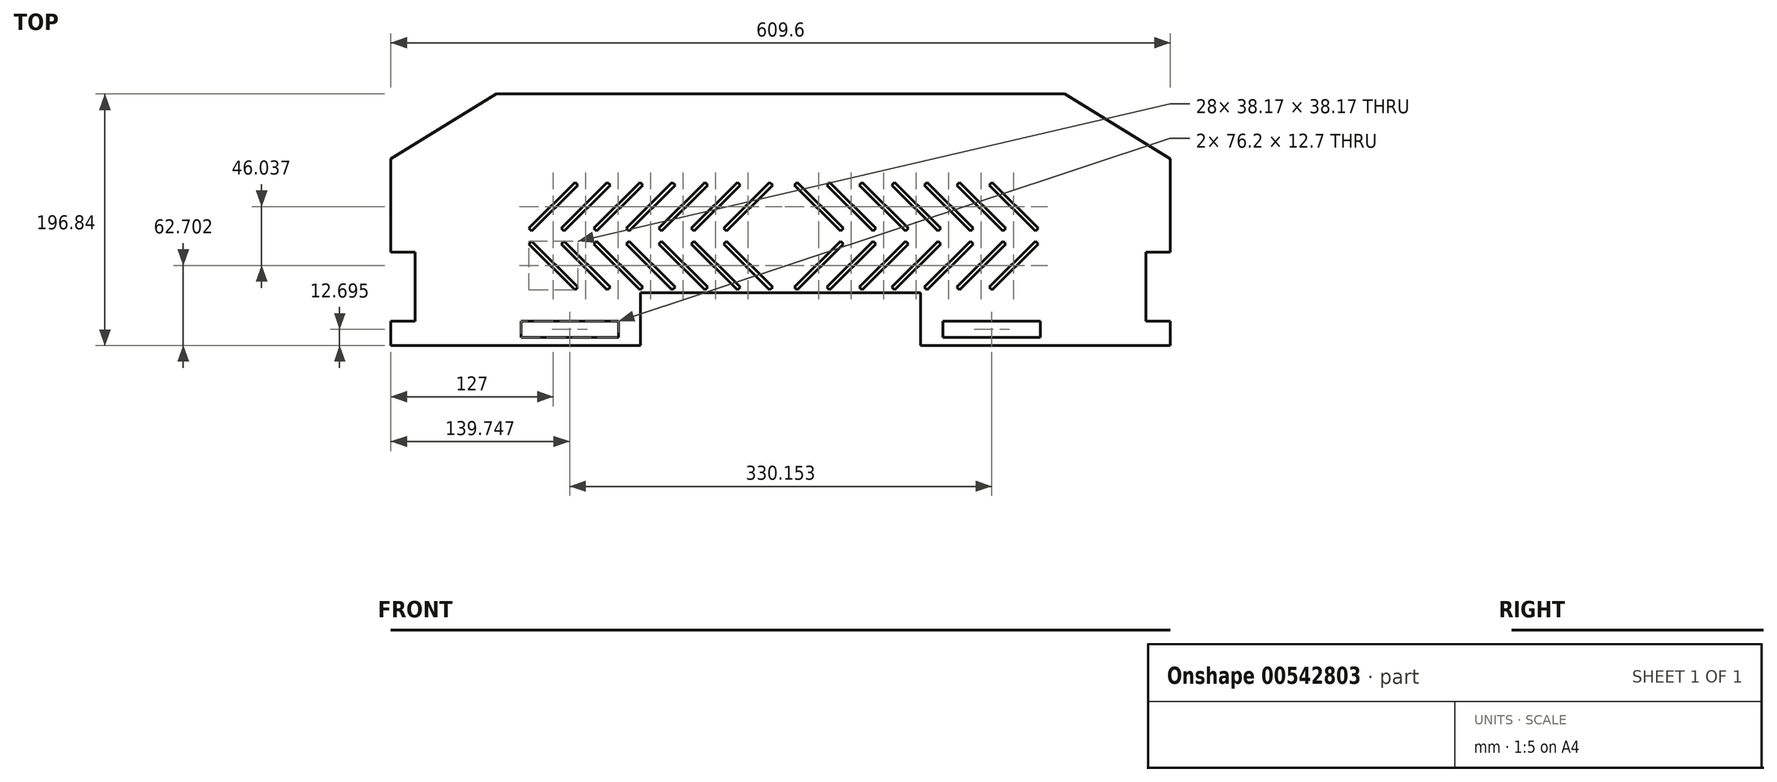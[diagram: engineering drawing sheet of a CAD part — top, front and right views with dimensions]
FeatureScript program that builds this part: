
annotation { "Feature Type Name" : "Feature", "Feature Type Description" : "" }
export const myFeature = defineFeature(function(context is Context, id is Id, definition is map)
    precondition{}
    {
        {
            var Q0;
            Q0=qCreatedBy(makeId("Top.planeOp"),FACE);
            var sketch = newSketch(context, id + "F0", { "sketchPlane" : qUnion([Q0])});
            skLineSegment(sketch, "E0", {"start": v(304.8, -19.05) * mm, "end": v(304.8, 53.97) * mm});
            skLineSegment(sketch, "E1", {"start": v(304.8, 53.97) * mm, "end": v(222.25, 104.77) * mm});
            skLineSegment(sketch, "E2", {"start": v(222.25, 104.77) * mm, "end": v(-222.25, 104.77) * mm});
            skLineSegment(sketch, "E3", {"start": v(-222.25, 104.77) * mm, "end": v(-304.8, 53.97) * mm});
            skLineSegment(sketch, "E4", {"start": v(-304.8, 53.97) * mm, "end": v(-304.8, -19.05) * mm});
            skLineSegment(sketch, "E5", {"start": v(-304.8, -19.05) * mm, "end": v(-285.75, -19.05) * mm});
            skLineSegment(sketch, "E6", {"start": v(-285.75, -19.05) * mm, "end": v(-285.75, -73.02) * mm});
            skLineSegment(sketch, "E7", {"start": v(-285.75, -73.02) * mm, "end": v(-304.8, -73.02) * mm});
            skLineSegment(sketch, "E8", {"start": v(-304.8, -73.02) * mm, "end": v(-304.8, -104.77) * mm});
            skLineSegment(sketch, "E9", {"start": v(-304.8, -104.77) * mm, "end": v(-109.54, -104.77) * mm});
            skLineSegment(sketch, "E10", {"start": v(-109.54, -104.77) * mm, "end": v(-109.54, -50.8) * mm});
            skLineSegment(sketch, "E11", {"start": v(-109.54, -50.8) * mm, "end": v(109.54, -50.8) * mm});
            skLineSegment(sketch, "E12", {"start": v(109.54, -50.8) * mm, "end": v(109.54, -104.77) * mm});
            skLineSegment(sketch, "E13", {"start": v(109.54, -104.77) * mm, "end": v(304.8, -104.77) * mm});
            skLineSegment(sketch, "E14", {"start": v(304.8, -104.77) * mm, "end": v(304.8, -73.02) * mm});
            skLineSegment(sketch, "E15", {"start": v(304.8, -73.02) * mm, "end": v(285.75, -73.02) * mm});
            skLineSegment(sketch, "E16", {"start": v(285.75, -73.02) * mm, "end": v(285.75, -19.05) * mm});
            skLineSegment(sketch, "E17", {"start": v(285.75, -19.05) * mm, "end": v(304.8, -19.05) * mm});
            skLineSegment(sketch, "E18", {"start": v(-126.95, -85.72) * mm, "end": v(-203.15, -85.72) * mm});
            skLineSegment(sketch, "E19", {"start": v(-203.15, -85.72) * mm, "end": v(-203.15, -73.02) * mm});
            skLineSegment(sketch, "E20", {"start": v(-203.15, -73.02) * mm, "end": v(-126.95, -73.02) * mm});
            skLineSegment(sketch, "E21", {"start": v(-126.95, -73.02) * mm, "end": v(-126.95, -85.72) * mm});
            skLineSegment(sketch, "E22", {"start": v(203.2, -85.72) * mm, "end": v(127, -85.72) * mm});
            skLineSegment(sketch, "E23", {"start": v(127, -85.72) * mm, "end": v(127, -73.02) * mm});
            skLineSegment(sketch, "E24", {"start": v(127, -73.02) * mm, "end": v(203.2, -73.02) * mm});
            skLineSegment(sketch, "E25", {"start": v(203.2, -73.02) * mm, "end": v(203.2, -85.72) * mm});
            skLineSegment(sketch, "E26", {"start": v(-194.64, -2.41) * mm, "end": v(-196.88, -0.17) * mm});
            skLineSegment(sketch, "E27", {"start": v(-196.88, -0.17) * mm, "end": v(-160.96, 35.75) * mm});
            skLineSegment(sketch, "E28", {"start": v(-160.96, 35.75) * mm, "end": v(-158.72, 33.5) * mm});
            skLineSegment(sketch, "E29", {"start": v(-158.72, 33.5) * mm, "end": v(-194.64, -2.41) * mm});
            skLineSegment(sketch, "E30", {"start": v(-169.24, -2.41) * mm, "end": v(-171.48, -0.17) * mm});
            skLineSegment(sketch, "E31", {"start": v(-171.48, -0.17) * mm, "end": v(-135.56, 35.75) * mm});
            skLineSegment(sketch, "E32", {"start": v(-135.56, 35.75) * mm, "end": v(-133.32, 33.5) * mm});
            skLineSegment(sketch, "E33", {"start": v(-133.32, 33.5) * mm, "end": v(-169.24, -2.41) * mm});
            skLineSegment(sketch, "E34", {"start": v(-143.84, -2.41) * mm, "end": v(-146.08, -0.17) * mm});
            skLineSegment(sketch, "E35", {"start": v(-146.08, -0.17) * mm, "end": v(-110.16, 35.75) * mm});
            skLineSegment(sketch, "E36", {"start": v(-110.16, 35.75) * mm, "end": v(-107.92, 33.5) * mm});
            skLineSegment(sketch, "E37", {"start": v(-107.92, 33.5) * mm, "end": v(-143.84, -2.41) * mm});
            skLineSegment(sketch, "E38", {"start": v(-118.44, -2.41) * mm, "end": v(-120.68, -0.17) * mm});
            skLineSegment(sketch, "E39", {"start": v(-120.68, -0.17) * mm, "end": v(-84.76, 35.75) * mm});
            skLineSegment(sketch, "E40", {"start": v(-84.76, 35.75) * mm, "end": v(-82.52, 33.5) * mm});
            skLineSegment(sketch, "E41", {"start": v(-82.52, 33.5) * mm, "end": v(-118.44, -2.41) * mm});
            skLineSegment(sketch, "E42", {"start": v(-93.04, -2.41) * mm, "end": v(-95.28, -0.17) * mm});
            skLineSegment(sketch, "E43", {"start": v(-95.28, -0.17) * mm, "end": v(-59.36, 35.75) * mm});
            skLineSegment(sketch, "E44", {"start": v(-59.36, 35.75) * mm, "end": v(-57.12, 33.5) * mm});
            skLineSegment(sketch, "E45", {"start": v(-57.12, 33.5) * mm, "end": v(-93.04, -2.41) * mm});
            skLineSegment(sketch, "E46", {"start": v(-67.64, -2.41) * mm, "end": v(-69.88, -0.17) * mm});
            skLineSegment(sketch, "E47", {"start": v(-69.88, -0.17) * mm, "end": v(-33.96, 35.75) * mm});
            skLineSegment(sketch, "E48", {"start": v(-33.96, 35.75) * mm, "end": v(-31.72, 33.5) * mm});
            skLineSegment(sketch, "E49", {"start": v(-31.72, 33.5) * mm, "end": v(-67.64, -2.41) * mm});
            skLineSegment(sketch, "E50", {"start": v(-42.24, -2.41) * mm, "end": v(-44.48, -0.17) * mm});
            skLineSegment(sketch, "E51", {"start": v(-44.48, -0.17) * mm, "end": v(-8.56, 35.75) * mm});
            skLineSegment(sketch, "E52", {"start": v(-8.56, 35.75) * mm, "end": v(-6.32, 33.5) * mm});
            skLineSegment(sketch, "E53", {"start": v(-6.32, 33.5) * mm, "end": v(-42.24, -2.41) * mm});
            skLineSegment(sketch, "E54", {"start": v(201.33, -0.17) * mm, "end": v(199.08, -2.41) * mm});
            skLineSegment(sketch, "E55", {"start": v(199.08, -2.41) * mm, "end": v(163.16, 33.5) * mm});
            skLineSegment(sketch, "E56", {"start": v(163.16, 33.5) * mm, "end": v(165.4, 35.75) * mm});
            skLineSegment(sketch, "E57", {"start": v(165.4, 35.75) * mm, "end": v(201.33, -0.17) * mm});
            skLineSegment(sketch, "E58", {"start": v(175.93, -0.17) * mm, "end": v(173.68, -2.41) * mm});
            skLineSegment(sketch, "E59", {"start": v(173.68, -2.41) * mm, "end": v(137.76, 33.5) * mm});
            skLineSegment(sketch, "E60", {"start": v(137.76, 33.5) * mm, "end": v(140, 35.75) * mm});
            skLineSegment(sketch, "E61", {"start": v(140, 35.75) * mm, "end": v(175.93, -0.17) * mm});
            skLineSegment(sketch, "E62", {"start": v(150.53, -0.17) * mm, "end": v(148.28, -2.41) * mm});
            skLineSegment(sketch, "E63", {"start": v(148.28, -2.41) * mm, "end": v(112.36, 33.5) * mm});
            skLineSegment(sketch, "E64", {"start": v(112.36, 33.5) * mm, "end": v(114.6, 35.75) * mm});
            skLineSegment(sketch, "E65", {"start": v(114.6, 35.75) * mm, "end": v(150.53, -0.17) * mm});
            skLineSegment(sketch, "E66", {"start": v(125.13, -0.17) * mm, "end": v(122.88, -2.41) * mm});
            skLineSegment(sketch, "E67", {"start": v(122.88, -2.41) * mm, "end": v(86.96, 33.5) * mm});
            skLineSegment(sketch, "E68", {"start": v(86.96, 33.5) * mm, "end": v(89.2, 35.75) * mm});
            skLineSegment(sketch, "E69", {"start": v(89.2, 35.75) * mm, "end": v(125.13, -0.17) * mm});
            skLineSegment(sketch, "E70", {"start": v(99.73, -0.17) * mm, "end": v(97.48, -2.41) * mm});
            skLineSegment(sketch, "E71", {"start": v(97.48, -2.41) * mm, "end": v(61.56, 33.5) * mm});
            skLineSegment(sketch, "E72", {"start": v(61.56, 33.5) * mm, "end": v(63.8, 35.75) * mm});
            skLineSegment(sketch, "E73", {"start": v(63.8, 35.75) * mm, "end": v(99.73, -0.17) * mm});
            skLineSegment(sketch, "E74", {"start": v(74.33, -0.17) * mm, "end": v(72.08, -2.41) * mm});
            skLineSegment(sketch, "E75", {"start": v(72.08, -2.41) * mm, "end": v(36.16, 33.5) * mm});
            skLineSegment(sketch, "E76", {"start": v(36.16, 33.5) * mm, "end": v(38.4, 35.75) * mm});
            skLineSegment(sketch, "E77", {"start": v(38.4, 35.75) * mm, "end": v(74.33, -0.17) * mm});
            skLineSegment(sketch, "E78", {"start": v(48.93, -0.17) * mm, "end": v(46.68, -2.41) * mm});
            skLineSegment(sketch, "E79", {"start": v(46.68, -2.41) * mm, "end": v(10.76, 33.5) * mm});
            skLineSegment(sketch, "E80", {"start": v(10.76, 33.5) * mm, "end": v(13, 35.75) * mm});
            skLineSegment(sketch, "E81", {"start": v(13, 35.75) * mm, "end": v(48.93, -0.17) * mm});
            skLineSegment(sketch, "E82", {"start": v(-194.64, -10.29) * mm, "end": v(-196.88, -12.53) * mm});
            skLineSegment(sketch, "E83", {"start": v(-196.88, -12.53) * mm, "end": v(-160.96, -48.45) * mm});
            skLineSegment(sketch, "E84", {"start": v(-160.96, -48.45) * mm, "end": v(-158.72, -46.2) * mm});
            skLineSegment(sketch, "E85", {"start": v(-158.72, -46.2) * mm, "end": v(-194.64, -10.29) * mm});
            skLineSegment(sketch, "E86", {"start": v(-169.24, -10.29) * mm, "end": v(-171.48, -12.53) * mm});
            skLineSegment(sketch, "E87", {"start": v(-171.48, -12.53) * mm, "end": v(-135.56, -48.45) * mm});
            skLineSegment(sketch, "E88", {"start": v(-135.56, -48.45) * mm, "end": v(-133.32, -46.2) * mm});
            skLineSegment(sketch, "E89", {"start": v(-133.32, -46.2) * mm, "end": v(-169.24, -10.29) * mm});
            skLineSegment(sketch, "E90", {"start": v(-143.84, -10.29) * mm, "end": v(-146.08, -12.53) * mm});
            skLineSegment(sketch, "E91", {"start": v(-146.08, -12.53) * mm, "end": v(-110.16, -48.45) * mm});
            skLineSegment(sketch, "E92", {"start": v(-110.16, -48.45) * mm, "end": v(-107.92, -46.2) * mm});
            skLineSegment(sketch, "E93", {"start": v(-107.92, -46.2) * mm, "end": v(-143.84, -10.29) * mm});
            skLineSegment(sketch, "E94", {"start": v(-118.44, -10.29) * mm, "end": v(-120.68, -12.53) * mm});
            skLineSegment(sketch, "E95", {"start": v(-120.68, -12.53) * mm, "end": v(-84.76, -48.45) * mm});
            skLineSegment(sketch, "E96", {"start": v(-84.76, -48.45) * mm, "end": v(-82.52, -46.2) * mm});
            skLineSegment(sketch, "E97", {"start": v(-82.52, -46.2) * mm, "end": v(-118.44, -10.29) * mm});
            skLineSegment(sketch, "E98", {"start": v(-93.04, -10.29) * mm, "end": v(-95.28, -12.53) * mm});
            skLineSegment(sketch, "E99", {"start": v(-95.28, -12.53) * mm, "end": v(-59.36, -48.45) * mm});
            skLineSegment(sketch, "E100", {"start": v(-59.36, -48.45) * mm, "end": v(-57.12, -46.2) * mm});
            skLineSegment(sketch, "E101", {"start": v(-57.12, -46.2) * mm, "end": v(-93.04, -10.29) * mm});
            skLineSegment(sketch, "E102", {"start": v(-67.64, -10.29) * mm, "end": v(-69.88, -12.53) * mm});
            skLineSegment(sketch, "E103", {"start": v(-69.88, -12.53) * mm, "end": v(-33.96, -48.45) * mm});
            skLineSegment(sketch, "E104", {"start": v(-33.96, -48.45) * mm, "end": v(-31.72, -46.2) * mm});
            skLineSegment(sketch, "E105", {"start": v(-31.72, -46.2) * mm, "end": v(-67.64, -10.29) * mm});
            skLineSegment(sketch, "E106", {"start": v(-42.24, -10.29) * mm, "end": v(-44.48, -12.53) * mm});
            skLineSegment(sketch, "E107", {"start": v(-44.48, -12.53) * mm, "end": v(-8.56, -48.45) * mm});
            skLineSegment(sketch, "E108", {"start": v(-8.56, -48.45) * mm, "end": v(-6.32, -46.2) * mm});
            skLineSegment(sketch, "E109", {"start": v(-6.32, -46.2) * mm, "end": v(-42.24, -10.29) * mm});
            skLineSegment(sketch, "E110", {"start": v(201.33, -12.53) * mm, "end": v(199.08, -10.29) * mm});
            skLineSegment(sketch, "E111", {"start": v(199.08, -10.29) * mm, "end": v(163.16, -46.2) * mm});
            skLineSegment(sketch, "E112", {"start": v(163.16, -46.2) * mm, "end": v(165.4, -48.45) * mm});
            skLineSegment(sketch, "E113", {"start": v(165.4, -48.45) * mm, "end": v(201.33, -12.53) * mm});
            skLineSegment(sketch, "E114", {"start": v(175.93, -12.53) * mm, "end": v(173.68, -10.29) * mm});
            skLineSegment(sketch, "E115", {"start": v(173.68, -10.29) * mm, "end": v(137.76, -46.2) * mm});
            skLineSegment(sketch, "E116", {"start": v(137.76, -46.2) * mm, "end": v(140, -48.45) * mm});
            skLineSegment(sketch, "E117", {"start": v(140, -48.45) * mm, "end": v(175.93, -12.53) * mm});
            skLineSegment(sketch, "E118", {"start": v(150.53, -12.53) * mm, "end": v(148.28, -10.29) * mm});
            skLineSegment(sketch, "E119", {"start": v(148.28, -10.29) * mm, "end": v(112.36, -46.2) * mm});
            skLineSegment(sketch, "E120", {"start": v(112.36, -46.2) * mm, "end": v(114.6, -48.45) * mm});
            skLineSegment(sketch, "E121", {"start": v(114.6, -48.45) * mm, "end": v(150.53, -12.53) * mm});
            skLineSegment(sketch, "E122", {"start": v(125.13, -12.53) * mm, "end": v(122.88, -10.29) * mm});
            skLineSegment(sketch, "E123", {"start": v(122.88, -10.29) * mm, "end": v(86.96, -46.2) * mm});
            skLineSegment(sketch, "E124", {"start": v(86.96, -46.2) * mm, "end": v(89.2, -48.45) * mm});
            skLineSegment(sketch, "E125", {"start": v(89.2, -48.45) * mm, "end": v(125.13, -12.53) * mm});
            skLineSegment(sketch, "E126", {"start": v(99.73, -12.53) * mm, "end": v(97.48, -10.29) * mm});
            skLineSegment(sketch, "E127", {"start": v(97.48, -10.29) * mm, "end": v(61.56, -46.2) * mm});
            skLineSegment(sketch, "E128", {"start": v(61.56, -46.2) * mm, "end": v(63.8, -48.45) * mm});
            skLineSegment(sketch, "E129", {"start": v(63.8, -48.45) * mm, "end": v(99.73, -12.53) * mm});
            skLineSegment(sketch, "E130", {"start": v(74.33, -12.53) * mm, "end": v(72.08, -10.29) * mm});
            skLineSegment(sketch, "E131", {"start": v(72.08, -10.29) * mm, "end": v(36.16, -46.2) * mm});
            skLineSegment(sketch, "E132", {"start": v(36.16, -46.2) * mm, "end": v(38.4, -48.45) * mm});
            skLineSegment(sketch, "E133", {"start": v(38.4, -48.45) * mm, "end": v(74.33, -12.53) * mm});
            skLineSegment(sketch, "E134", {"start": v(48.93, -12.53) * mm, "end": v(46.68, -10.29) * mm});
            skLineSegment(sketch, "E135", {"start": v(46.68, -10.29) * mm, "end": v(10.76, -46.2) * mm});
            skLineSegment(sketch, "E136", {"start": v(10.76, -46.2) * mm, "end": v(13, -48.45) * mm});
            skLineSegment(sketch, "E137", {"start": v(13, -48.45) * mm, "end": v(48.93, -12.53) * mm});
            skLineSegment(sketch, "E138", {"start": v(244.47, -67.47) * mm, "end": v(-244.48, -67.47) * mm});
            skLineSegment(sketch, "E139", {"start": v(-244.48, -67.47) * mm, "end": v(-244.48, -46.83) * mm});
            skLineSegment(sketch, "E140", {"start": v(-244.48, -46.83) * mm, "end": v(244.47, -46.83) * mm});
            skLineSegment(sketch, "E141", {"start": v(244.47, -46.83) * mm, "end": v(244.47, -67.47) * mm});
            skSolve(sketch);
        }
        {
            var Q0;
            Q0=makeQuery(id+"F0.imprint","IMPRINT",FACE,{"disambiguationData":[TD([[makeQuery(id+"F0.imprint","IMPRINT",EDGE,{"derivedFrom":sQuery(id+"F0.wireOp",EDGE,"E0")}),1.0]])]});
            var Q1;
            {var subQ50=sQuery(id+"F0.wireOp",EDGE,"E11");Q1=makeQuery(id+"F0.imprint","IMPRINT",FACE,{"disambiguationData":[TD([[makeQuery(id+"F0.imprint","IMPRINT",EDGE,{"derivedFrom":subQ50}),1.0]])]});}
            extrude(context, id + "F1", {"entities" : qUnion([Q0, Q1]), "depth" : 1 / 203.2 * mm});
        }
        {
            var Q0;
            Q0=makeQuery(id+"F1.opExtrude","SWEPT_FACE",FACE,{"disambiguationData":[OSD([sQuery(id+"F0.wireOp",EDGE,"E9")])]});
            var Q1;
            Q1=makeQuery(id+"F1.opExtrude","SWEPT_FACE",FACE,{"disambiguationData":[OSD([sQuery(id+"F0.wireOp",EDGE,"E13")])]});
            extrude(context, id + "F2", {"entities" : qUnion([Q0, Q1]), "operationType" : NewBodyOperationType.REMOVE, "oppositeDirection" : true, "depth" : 12.7 * mm, "offsetDistance" : 25.4 * mm});
        }
    });
